# Revit family: PRD_FrankeWS_ShwrHds_DrenchShower_SHHE0004
name_source: partatom
category: Plumbing Fixtures
revit_build: Autodesk Revit 2018 (Build: 20190510_1515(x64)
units: mm (PartAtom-declared; Revit-internal decimal feet)

## family parameters
Cut with Voids When Loaded = Yes
Host = Face
OmniClass Number = 23.45.05.14.17
OmniClass Title = Showers
Part Type = Normal
Room Calculation Point = No
Round Connector Dimension = Use Diameter
Shared = Yes

## types (1)
- SHHE0004
    AdjustableTiltAngle = Yes
    AssetType = Fixed
    BIMObjectName = PRD_AR_ShowerHeads_DrenchShower_SHHE0004
    Category = Pr_40_20_87_76, Shower heads
    Default Elevation = 2000 mm  [stored 6.56168 ft]
    Description = Drench shower DN 15 with ball joint for wall mounting. With shower head, projection 120 mm and rosette. Adjustable spray angle 28°. Chromium-plated brass. Volume flow 61.8 l/min at 3 bar flow pressure
    DiameterNominal = 15  [stored 0.0492126 ft]
    DrainSize = 15 mm  [stored 0.0492126 ft]
    DurationUnit = year
    Features = With shower head, projection 120 mm and rosette
    Finish = chromium-plated
    Flow = 1.0 L/s
    GrossWeight = 0.60 kg
    HasTray = FALSE
    IfcExportAs = IfcSanitaryTerminalType
    IfcExportType = SHOWER
    InletSize = DN 15
    Manufacturer = KWC Group AG
    ManufacturerName = KWC Group AG
    ManufacturerURL = www.kwc.com
    Material = brass
    MinimumFlowPressure = 1.00 bar
    Model = SHHE0004
    ModelNumber = 2030034417
    ModelReference = SHHE0004
    NBSDescription = Shower heads
    NBSReference = 45-35-70/333
    Name = Drench shower SHHE0004
    NetWeight = 0.57 kg
    NominalDepth = 0 mm  [stored 0 ft]
    NominalHeight = 0 mm  [stored 0 ft]
    NominalWidth = 85 mm  [stored 0.278871 ft]
    ProductCode = 210.0597.539
    ProductInformation = https://pim.kwc.com
    ShowerHeadDescription = Drench shower head
    ShowerMaterial = PRD_AR_ChromatedBrass_HighPolished
    ShowerType = Individual
    SoundInsulation = No
    SpoutProjection = 120.00 mm
    TailorMade = No
    Type = Shower head
    TypeOfConnection = Wall connection
    TypeOfShowerHead = Drench shower head
    URL = www.kwc.com
    Uniclass2015Code = Pr_40_20_87_76
    Uniclass2015Title = Shower heads
    Uniclass2015Version = Products v1.23
    Version = 1
    VolumeFlowRate = 1.03 l/s at 3 bar
    WarrantyDurationUnit = year

note: [stored X ft] marks values corroborated as IEEE doubles in the binary element streams (Revit-internal decimal feet)

## geometry (parser evidence)
native form markers: Sweep x2
no freeform markers — native parametric forms only
